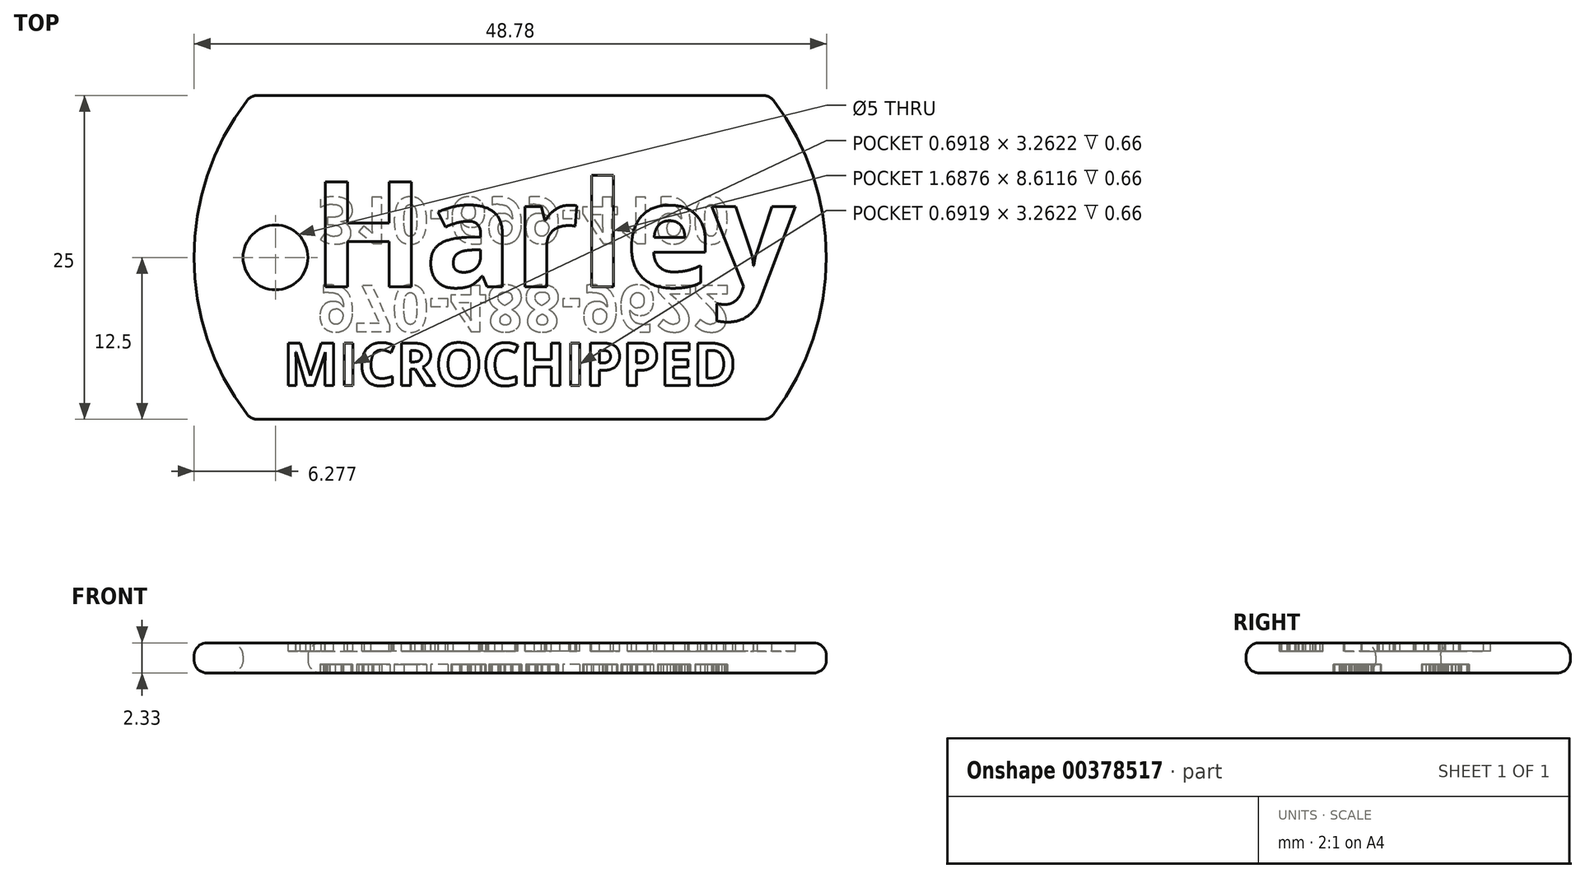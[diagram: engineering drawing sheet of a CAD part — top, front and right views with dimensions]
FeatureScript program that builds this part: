
annotation { "Feature Type Name" : "Feature", "Feature Type Description" : "" }
export const myFeature = defineFeature(function(context is Context, id is Id, definition is map)
    precondition{}
    {
        {
            var Q0;
            Q0=qCreatedBy(makeId("Top.planeOp"),FACE);
            var sketch = newSketch(context, id + "F0", { "sketchPlane" : qUnion([Q0])});
            skLineSegment(sketch, "E0.bottom", {"start": v(-20, 12.5) * mm, "end": v(20, 12.5) * mm});
            skLineSegment(sketch, "E0.top", {"start": v(-20, -12.5) * mm, "end": v(20, -12.5) * mm});
            skArc(sketch, "E1", {"start": v(-20, 12.5) * mm, "mid": v(-24.39, 0) * mm, "end": v(-20, -12.5) * mm});
            skArc(sketch, "E2", {"start": v(20, -12.5) * mm, "mid": v(24.39, 0) * mm, "end": v(20, 12.5) * mm});
            skCircle(sketch, "E3", {"center": v(-18.11, 0) * mm, "radius": 2.5 * mm});
            skSolve(sketch);
        }
        {
            var Q0;
            Q0=makeQuery(id+"F0.imprint","IMPRINT",FACE,{"disambiguationData":[TD([[makeQuery(id+"F0.imprint","IMPRINT",EDGE,{"derivedFrom":sQuery(id+"F0.wireOp",EDGE,"E0.bottom")}),-1.0]])]});
            extrude(context, id + "F1", {"entities" : qUnion([Q0]), "flatOperationType" : FlatOperationType.REMOVE, "offsetDistance" : 25 * mm, "depth" : 2.33 * mm, "domain" : OperationDomain.MODEL});
        }
        {
            var Q0;
            Q0=makeQuery(id+"F1.opExtrude","CAP_FACE",FACE,{"disambiguationData":[OSD([sQuery(id+"F0.wireOp",EDGE,"E0.bottom"),sQuery(id+"F0.wireOp",EDGE,"E0.top"),sQuery(id+"F0.wireOp",EDGE,"E1"),sQuery(id+"F0.wireOp",EDGE,"E2"),sQuery(id+"F0.wireOp",EDGE,"E3")])],"isStart":false});
            var sketch = newSketch(context, id + "F2", { "sketchPlane" : qUnion([Q0])});
            skText(sketch, "E4", { "text": "Harley", "fontName": "OpenSans-Bold.ttf"});
            skText(sketch, "E5", { "text": "MICROCHIPPED", "fontName": "OpenSans-Bold.ttf"});
            const initialGuessF2  = {"E4": [-0.01528, -0.00227, 1, 0, 0.00816], "E5": [-0.01754, -0.00988, 1, 0, 0.00329]};
            skSetInitialGuess(sketch, initialGuessF2);
            skSolve(sketch);
        }
        {
            var Q0;
            Q0=qSketchRegion(id+"F2",true);
            extrude(context, id + "F3", {"entities" : qUnion([Q0]), "operationType" : NewBodyOperationType.REMOVE, "flatOperationType" : FlatOperationType.REMOVE, "oppositeDirection" : true, "offsetDistance" : 25 * mm, "depth" : 0.66 * mm, "domain" : OperationDomain.MODEL});
        }
        {
            var Q0;
            Q0=makeQuery(id+"F1.opExtrude","SWEPT_FACE",FACE,{"disambiguationData":[OSD([sQuery(id+"F0.wireOp",EDGE,"E2")])]});
            var Q1;
            Q1=makeQuery(id+"F1.opExtrude","SWEPT_FACE",FACE,{"disambiguationData":[OSD([sQuery(id+"F0.wireOp",EDGE,"E0.top")])]});
            var Q2;
            Q2=makeQuery(id+"F1.opExtrude","SWEPT_FACE",FACE,{"disambiguationData":[OSD([sQuery(id+"F0.wireOp",EDGE,"E3")])]});
            var Q3;
            Q3=makeQuery(id+"F1.opExtrude","SWEPT_FACE",FACE,{"disambiguationData":[OSD([sQuery(id+"F0.wireOp",EDGE,"E1")])]});
            var Q4;
            Q4=makeQuery(id+"F1.opExtrude","SWEPT_FACE",FACE,{"disambiguationData":[OSD([sQuery(id+"F0.wireOp",EDGE,"E0.bottom")])]});
            fillet(context, id + "F4", {"entities" : qUnion([Q0, Q1, Q2, Q3, Q4]), "radius" : 1 * mm, "tangentPropagation" : true, "allowEdgeOverflow" : false});
        }
        {
            var Q0;
            Q0=makeQuery(id+"F1.opExtrude","CAP_FACE",FACE,{"disambiguationData":[OSD([sQuery(id+"F0.wireOp",EDGE,"E0.bottom"),sQuery(id+"F0.wireOp",EDGE,"E0.top"),sQuery(id+"F0.wireOp",EDGE,"E1"),sQuery(id+"F0.wireOp",EDGE,"E2"),sQuery(id+"F0.wireOp",EDGE,"E3")])],"isStart":true});
            var sketch = newSketch(context, id + "F5", { "sketchPlane" : qUnion([Q0])});
            skText(sketch, "E6", { "text": "970-488-9622\n310-699-4190", "fontName": "OpenSans-Bold.ttf"});
            const initialGuessF5  = {"E6": [-0.01484, 0.00216, 1, 0, 0.0036]};
            skSetInitialGuess(sketch, initialGuessF5);
            skSolve(sketch);
        }
        {
            var Q0;
            Q0 = qSketchRegion(id + "F5", true);
            extrude(context, id + "F6", {"entities" : qUnion([Q0]), "operationType" : NewBodyOperationType.REMOVE, "flatOperationType" : FlatOperationType.REMOVE, "oppositeDirection" : true, "offsetDistance" : 25 * mm, "depth" : 0.66 * mm, "domain" : OperationDomain.MODEL});
        }
    });
